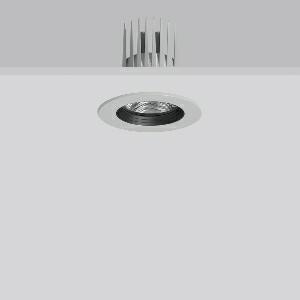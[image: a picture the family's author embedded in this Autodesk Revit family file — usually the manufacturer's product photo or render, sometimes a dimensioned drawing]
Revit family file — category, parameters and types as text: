
# Revit family: heledon_mini_e_901749_004_2_cc40
name_source: partatom
category: Lighting Fixtures
units: mm (PartAtom-declared; Revit-internal decimal feet)

## family parameters
Cut with Voids When Loaded = No
Host = Face
Light Source = No
Part Type = Normal
Room Calculation Point = No
Round Connector Dimension = Use Diameter
Shared = No

## types (1)
- HELEDON mini E (1 x LED Modul 927, 3300 lm, 2700)
    Apparent Load = 29 VA
    Approval mark = CE
    CIE Flux Codes = 99 100 100 100 100
    Color Rendering = 92
    Color Temperature = 2700
    Default Elevation = 1800 mm
    Description = Series: HELEDON mini
Round recessed downlight. Housing: die-cast aluminium, powder-coated. Black plastic ring and recessed LED to prevent glare from the side. Optical assembly with reflector made of MIRO-Silver with 98% total light reflection for outstanding efficiency - can be changed without tools. Best colour rendering index Ra>90. Suitable for Recessed ceiling mounting. Installation without tools thanks to spring fastening system. Including separate LED converter with connecting cable 600 mm.High quality converter without flickering and stroboscopic effect. Through-wiring box (5 pole) available as accessory. The following accessories can be mounted without use of tools: interchangeable lenses, decorative glasses, honeycomb louvre, clear and frosted diffusers, white interchangeable plastic ring. 
Colour: silver
Diameter: 124 mm
Height: 3 mm
Cut-out diameter: 114 mm
Recess height: 170 mm
Luminaire: recess height: 120 mm
Lamp: LED
Socket: without socket
Colour temperature: 2700K
Colour rendering index (CRI): 92
System power: 29 W
Rated luminous flux: 3300 lm
Luminous efficiency: 114 lm/W
Control gear: Regulated power supply
Protection class: II
Type of protection: IP 20
    Height = 0 mm  [stored 0 ft]
    Lamp = 1 x LED Modul 927
    Lamp Light Flux = 3300 lm
    Lamp count = 1
    Length = 124 mm  [stored 0.406824 ft]
    Lifetime = 50000 h
    Luminous efficacy = 114 lm/W
    Manufacturer = RZB
    ModVariant = No
    Model = 901749.004.2
    Mounting Place = Ceiling
    Mounting Type = Recessed
    Number of Poles = 1
    OnlyDefault = Yes
    Power Factor = 1
    Product Name = HELEDON mini E
    Product group = Recessed downlights
    ProductGroupID = 402
    Protection Class = Protection class II
    Protection Degree = IP 20
    RLX_Detail_Level = 1
    RLX_Emergency_Light_Flux = 0 lm
    RLX_Emergency_Type = 0
    RLX_Emergency_Type_DB = No
    RlxData = <blob elided: 127097 chars, md5=5060dae0>
    Socket = socket
    Standby Power = 0 W
    System Light Flux = 3300 lm
    System Power = 29 W
    Type Comments = Product without accessories
    Type Image = 901657.004.jpg
    URL = http://relux.com
    VarID = ---
    Voltage = 230 V
    Voltage Range = 220-240 V
    Weight = 0.00 kg
    Width = 0 mm  [stored 0 ft]

note: [stored X ft] marks values corroborated as IEEE doubles in the binary element streams (Revit-internal decimal feet)

## geometry (parser evidence)
native form markers: Blend x4, Sweep x13
no freeform markers — native parametric forms only
